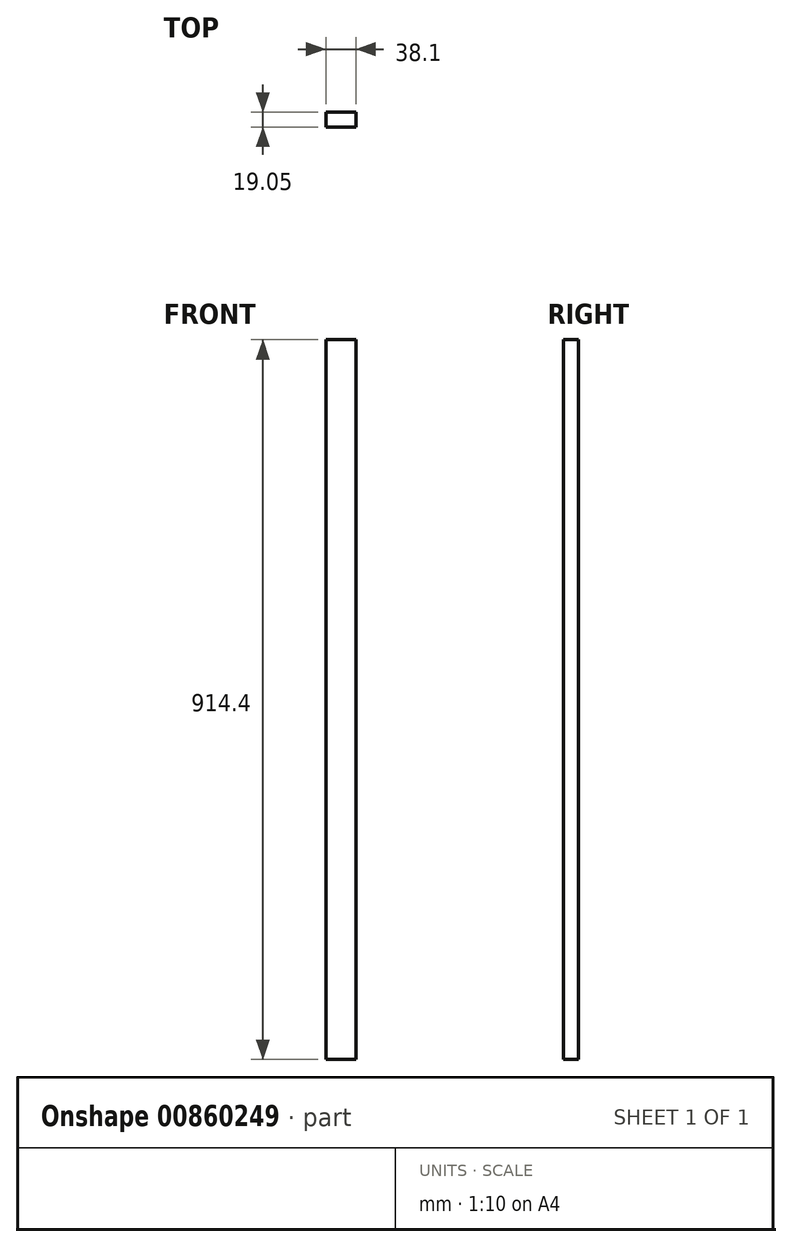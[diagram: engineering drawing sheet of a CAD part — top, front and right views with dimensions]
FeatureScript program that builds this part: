
annotation { "Feature Type Name" : "Feature", "Feature Type Description" : "" }
export const myFeature = defineFeature(function(context is Context, id is Id, definition is map)
    precondition{}
    {
        {
            var Q0;
            Q0=qCreatedBy(makeId("Front.planeOp"),FACE);
            var sketch = newSketch(context, id + "F0", { "sketchPlane" : qUnion([Q0])});
            skLineSegment(sketch, "E0.bottom", {"start": v(19.05, -457.2) * mm, "end": v(-19.05, -457.2) * mm});
            skLineSegment(sketch, "E0.top", {"start": v(19.05, 457.2) * mm, "end": v(-19.05, 457.2) * mm});
            skLineSegment(sketch, "E0.left", {"start": v(19.05, -457.2) * mm, "end": v(19.05, 457.2) * mm});
            skLineSegment(sketch, "E0.right", {"start": v(-19.05, -457.2) * mm, "end": v(-19.05, 457.2) * mm});
            skPoint(sketch, "E0.middle", {"position": v(0, 0) * mm});
            skSolve(sketch);
        }
        {
            var Q0;
            Q0 = qSketchRegion(id + "F0", true);
            extrude(context, id + "F1", {"entities" : qUnion([Q0]), "depth" : 19.05 * mm, "offsetDistance" : 25.4 * mm});
        }
    });
